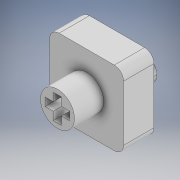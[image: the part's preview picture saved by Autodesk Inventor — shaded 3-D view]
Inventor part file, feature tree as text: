
AUTODESK INVENTOR PART (.ipt)
format: ipt  version: 2022 (Build 260153000, 153)  size: 315,392 bytes
history: native  units: in
note: dims shown in document units (in); Inventor stores cm internally (conversion verified against a paired STEP export)
features: sketch x4, extrude x3, plane x1, projected_geometry x1
ambient origin geometry x8: Origin, YZ Plane, XZ Plane, XY Plane, X Axis, Y Axis, Z Axis, Center Point
bodies: Body1 (feature_tree)
feature tree (9):
  sketch  "Sketch1"  dims[d3=0.2205in d4=0.1594in]
  plane  "Work Plane1"
  sketch  "Sketch2"  dims[d5=0.0531in d6=0.1594in]
  extrude  "Extrusion3"  Depth=0.1594in
  extrude  "Extrusion4"  Depth=0.1594in
  extrude  "Extrusion5"  Depth=0.5016in
  projected_geometry  "Projected Loop1"
  sketch  "Sketch3"  dims[d7=0.0531in d10=0.5016in]
  sketch  "Sketch4"  dims[d12=0.1969in d13=0.0in d14=0.2205in d15=0.1594in d16=0.0531in d17=0.1594in d18=0.0531in d19=0.189in d20=0.0in d21=0.0892in d22=0.2693in d23=0.0354in d24=0.0in]
